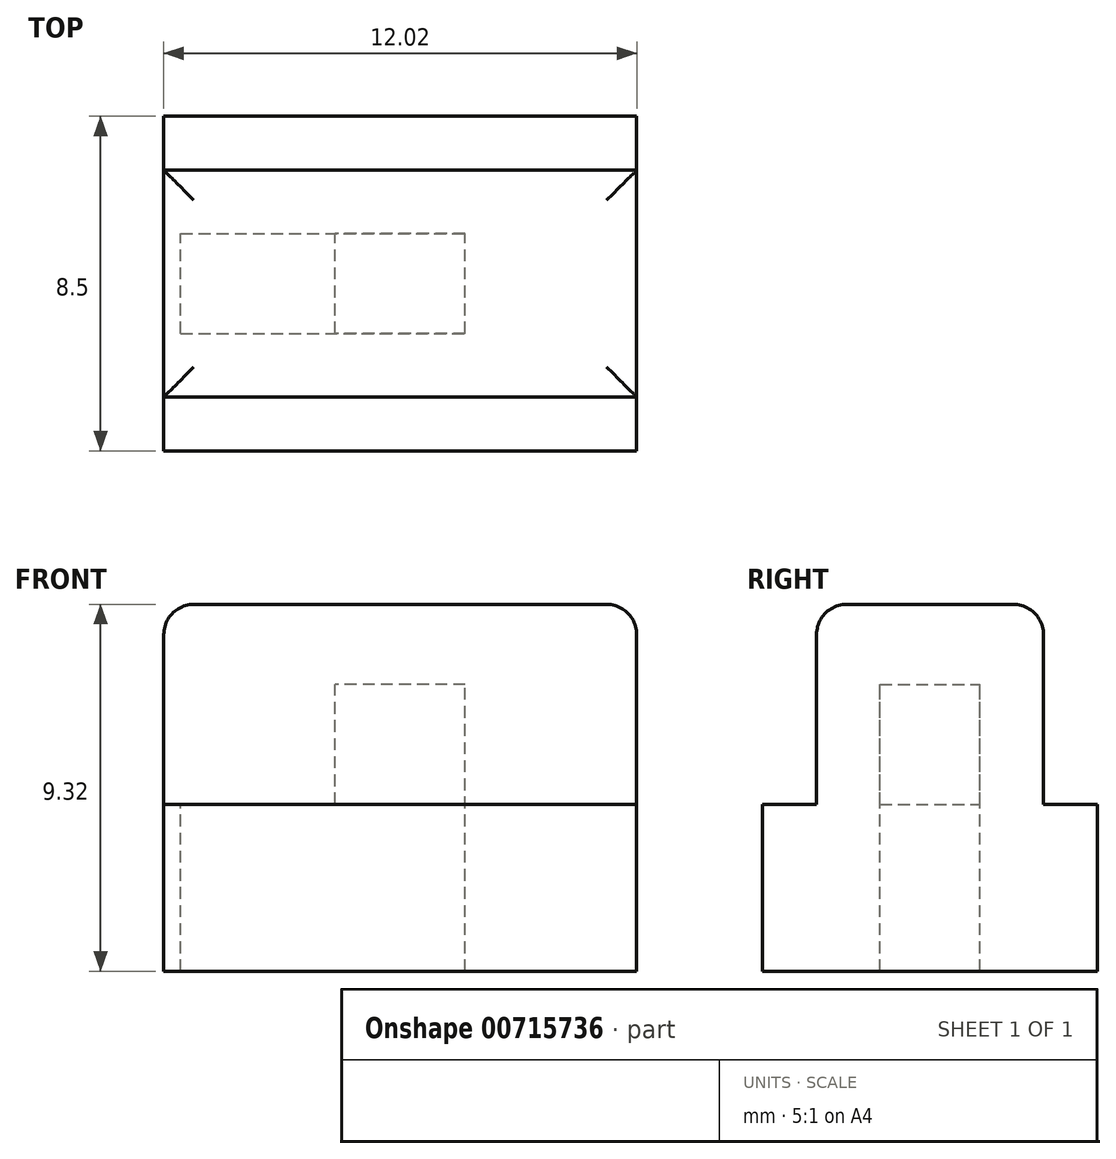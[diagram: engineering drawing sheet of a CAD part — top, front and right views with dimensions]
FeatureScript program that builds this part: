
annotation { "Feature Type Name" : "Feature", "Feature Type Description" : "" }
export const myFeature = defineFeature(function(context is Context, id is Id, definition is map)
    precondition{}
    {
        {
            var Q0;
            Q0=qCreatedBy(makeId("Top.planeOp"),FACE);
            var sketch = newSketch(context, id + "F0", { "sketchPlane" : qUnion([Q0])});
            skLineSegment(sketch, "E0.bottom", {"start": v(6, 2.88) * mm, "end": v(-6, 2.88) * mm});
            skLineSegment(sketch, "E0.top", {"start": v(6, -2.88) * mm, "end": v(-6, -2.88) * mm});
            skLineSegment(sketch, "E0.left", {"start": v(6, 2.88) * mm, "end": v(6, -2.88) * mm});
            skLineSegment(sketch, "E0.right", {"start": v(-6, 2.88) * mm, "end": v(-6, -2.88) * mm});
            skPoint(sketch, "E0.middle", {"position": v(0, 0) * mm});
            skSolve(sketch);
        }
        {
            var Q0;
            Q0=makeQuery(id+"F0.imprint","IMPRINT",FACE,{"disambiguationData":[TD([[makeQuery(id+"F0.imprint","IMPRINT",EDGE,{"derivedFrom":sQuery(id+"F0.wireOp",EDGE,"E0.bottom")}),1.0]])]});
            extrude(context, id + "F1", {"entities" : qUnion([Q0]), "depth" : 5.08 * mm, "offsetDistance" : 25.4 * mm});
        }
        {
            var Q0;
            Q0=qCreatedBy(makeId("Top.planeOp"),FACE);
            var sketch = newSketch(context, id + "F2", { "sketchPlane" : qUnion([Q0])});
            skLineSegment(sketch, "E1.bottom", {"start": v(6, -4.25) * mm, "end": v(-6, -4.25) * mm});
            skLineSegment(sketch, "E1.top", {"start": v(6, 4.25) * mm, "end": v(-6, 4.25) * mm});
            skLineSegment(sketch, "E1.left", {"start": v(6, -4.25) * mm, "end": v(6, 4.25) * mm});
            skLineSegment(sketch, "E1.right", {"start": v(-6, -4.25) * mm, "end": v(-6, 4.25) * mm});
            skPoint(sketch, "E1.middle", {"position": v(0, 0) * mm});
            skSolve(sketch);
        }
        {
            var Q0;
            Q0=makeQuery(id+"F2.imprint","IMPRINT",FACE,{"disambiguationData":[TD([[makeQuery(id+"F2.imprint","IMPRINT",EDGE,{"derivedFrom":sQuery(id+"F2.wireOp",EDGE,"E1.bottom")}),-1.0]])]});
            extrude(context, id + "F3", {"entities" : qUnion([Q0]), "operationType" : NewBodyOperationType.ADD, "oppositeDirection" : true, "depth" : 4.24 * mm, "offsetDistance" : 25.4 * mm});
        }
        {
            var Q0;
            Q0=makeQuery(id+"F1.opExtrude","CAP_FACE",FACE,{"disambiguationData":[OSD([sQuery(id+"F0.wireOp",EDGE,"E0.bottom"),sQuery(id+"F0.wireOp",EDGE,"E0.top"),sQuery(id+"F0.wireOp",EDGE,"E0.left"),sQuery(id+"F0.wireOp",EDGE,"E0.right")])],"isStart":false});
            fillet(context, id + "F4", {"entities" : qUnion([Q0]), "radius" : 0.76 * mm, "tangentPropagation" : true, "allowEdgeOverflow" : false});
        }
        {
            var Q0;
            Q0=qCreatedBy(makeId("Top.planeOp"),FACE);
            var sketch = newSketch(context, id + "F5", { "sketchPlane" : qUnion([Q0])});
            skLineSegment(sketch, "E2.bottom", {"start": v(1.65, -1.27) * mm, "end": v(-1.65, -1.27) * mm});
            skLineSegment(sketch, "E2.top", {"start": v(1.65, 1.27) * mm, "end": v(-1.65, 1.27) * mm});
            skLineSegment(sketch, "E2.left", {"start": v(1.65, -1.27) * mm, "end": v(1.65, 1.27) * mm});
            skLineSegment(sketch, "E2.right", {"start": v(-1.65, -1.27) * mm, "end": v(-1.65, 1.27) * mm});
            skPoint(sketch, "E2.middle", {"position": v(0, 0) * mm});
            skSolve(sketch);
        }
        {
            var Q0;
            Q0=qCreatedBy(makeId("Top.planeOp"),FACE);
            var sketch = newSketch(context, id + "F6", { "sketchPlane" : qUnion([Q0])});
            skLineSegment(sketch, "E3.bottom", {"start": v(-5.58, -1.27) * mm, "end": v(-1.4, -1.27) * mm});
            skLineSegment(sketch, "E3.top", {"start": v(-5.58, 1.27) * mm, "end": v(-1.4, 1.27) * mm});
            skLineSegment(sketch, "E3.left", {"start": v(-5.58, -1.27) * mm, "end": v(-5.58, 1.27) * mm});
            skLineSegment(sketch, "E3.right", {"start": v(-1.4, -1.27) * mm, "end": v(-1.4, 1.27) * mm});
            skSolve(sketch);
        }
        {
            var Q0;
            Q0=makeQuery(id+"F6.imprint","IMPRINT",FACE,{"disambiguationData":[TD([[makeQuery(id+"F6.imprint","IMPRINT",EDGE,{"derivedFrom":sQuery(id+"F6.wireOp",EDGE,"E3.bottom")}),1.0]])]});
            extrude(context, id + "F7", {"entities" : qUnion([Q0]), "operationType" : NewBodyOperationType.REMOVE, "oppositeDirection" : true, "depth" : 4.24 * mm, "offsetDistance" : 25.4 * mm});
        }
        {
            var Q0;
            Q0=makeQuery(id+"F5.imprint","IMPRINT",FACE,{"disambiguationData":[TD([[makeQuery(id+"F5.imprint","IMPRINT",EDGE,{"derivedFrom":sQuery(id+"F5.wireOp",EDGE,"E2.bottom")}),-1.0]])]});
            extrude(context, id + "F8", {"entities" : qUnion([Q0]), "operationType" : NewBodyOperationType.REMOVE, "oppositeDirection" : true, "depth" : 4.32 * mm, "offsetDistance" : 25.4 * mm, "hasSecondDirection" : true, "secondDirectionOppositeDirection" : false, "secondDirectionDepth" : 3.05 * mm});
        }
    });
